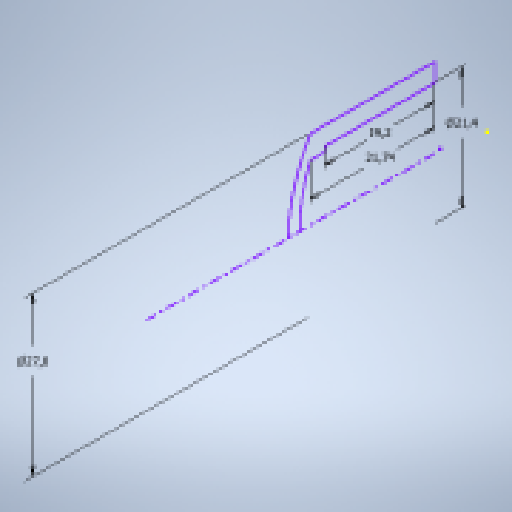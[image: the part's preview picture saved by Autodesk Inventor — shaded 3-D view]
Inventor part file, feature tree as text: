
AUTODESK INVENTOR PART (.ipt)
format: ipt  version: 2023.1 (Build 271208000, 208)  size: 194,048 bytes
history: native  units: mm
features: sketch x2, revolve x1, extrude x1
ambient origin geometry x8: Origin, YZ Plane, XZ Plane, XY Plane, X Axis, Y Axis, Z Axis, Center Point
bodies: Solid1 (feature_tree)
feature tree (4):
  revolve  "Revolution1"  [1 undecoded]
  extrude  "Extrusion1"  Depth=5.0mm
  sketch  "Sketch1"  dims[d1=27.8mm d3=19.2mm]
  sketch  "Sketch2"  dims[d4=21.74mm d5=21.4mm d6=25.6mm d7=90.0deg d8=31.3mm d9=5.0mm d10=0.0mm]
note: 1 required parameter value undecoded (feature->parameter linkage not recoverable at this tier; creation-order binding heuristic only, values carry confidence <= 0.55)
